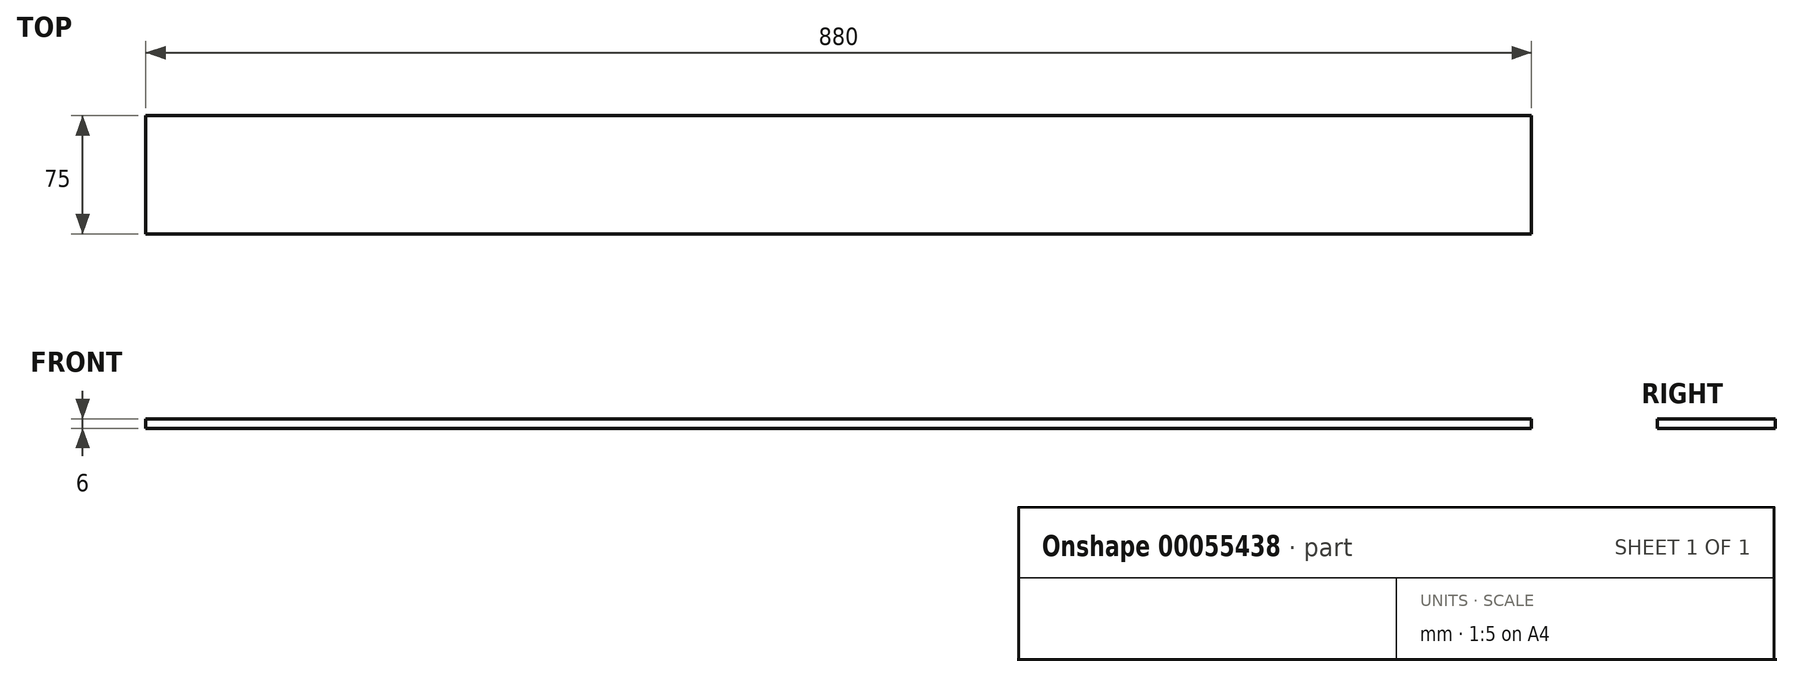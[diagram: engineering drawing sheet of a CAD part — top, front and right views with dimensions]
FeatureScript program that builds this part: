
annotation { "Feature Type Name" : "Feature", "Feature Type Description" : "" }
export const myFeature = defineFeature(function(context is Context, id is Id, definition is map)
    precondition{}
    {
        {
            var Q0;
            Q0=qCreatedBy(makeId("Top.planeOp"),FACE);
            var sketch = newSketch(context, id + "F0", { "sketchPlane" : qUnion([Q0])});
            skLineSegment(sketch, "E0.bottom", {"start": v(0, 0) * mm, "end": v(880, 0) * mm});
            skLineSegment(sketch, "E0.top", {"start": v(0, 75) * mm, "end": v(880, 75) * mm});
            skLineSegment(sketch, "E0.left", {"start": v(0, 0) * mm, "end": v(0, 75) * mm});
            skLineSegment(sketch, "E0.right", {"start": v(880, 0) * mm, "end": v(880, 75) * mm});
            skSolve(sketch);
        }
        {
            var Q0;
            Q0 = qSketchRegion(id + "F0", true);
            extrude(context, id + "F1", {"entities" : qUnion([Q0]), "depth" : 6 * mm});
        }
    });
